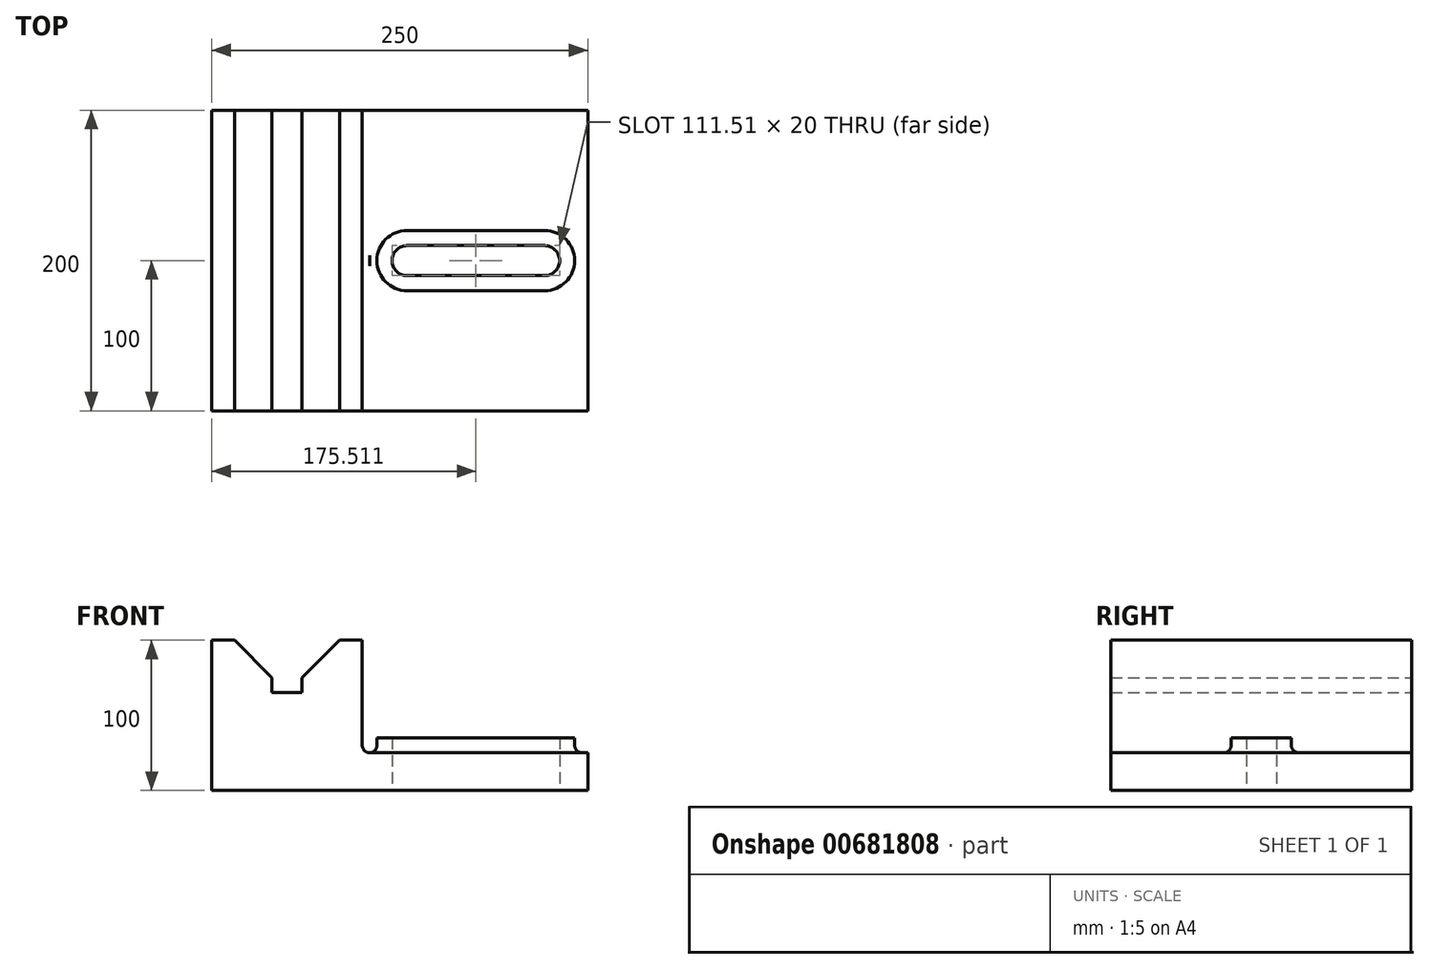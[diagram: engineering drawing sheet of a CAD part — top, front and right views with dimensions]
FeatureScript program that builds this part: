
annotation { "Feature Type Name" : "Feature", "Feature Type Description" : "" }
export const myFeature = defineFeature(function(context is Context, id is Id, definition is map)
    precondition{}
    {
        {
            var Q0;
            Q0=qCreatedBy(makeId("Front.planeOp"),FACE);
            var sketch = newSketch(context, id + "F0", { "sketchPlane" : qUnion([Q0])});
            skLineSegment(sketch, "E0", {"start": v(0, 0) * mm, "end": v(-250, 0) * mm});
            skLineSegment(sketch, "E1", {"start": v(-250, 0) * mm, "end": v(-250, 100) * mm});
            skLineSegment(sketch, "E2", {"start": v(-250, 100) * mm, "end": v(-235, 100) * mm});
            skLineSegment(sketch, "E3", {"start": v(-235, 100) * mm, "end": v(-210, 75) * mm});
            skLineSegment(sketch, "E4", {"start": v(-210, 75) * mm, "end": v(-210, 65) * mm});
            skLineSegment(sketch, "E5", {"start": v(-210, 65) * mm, "end": v(-190, 65) * mm});
            skLineSegment(sketch, "E6", {"start": v(-190, 65) * mm, "end": v(-190, 75) * mm});
            skLineSegment(sketch, "E7", {"start": v(-190, 75) * mm, "end": v(-165, 100) * mm});
            skLineSegment(sketch, "E8", {"start": v(-165, 100) * mm, "end": v(-150, 100) * mm});
            skLineSegment(sketch, "E9", {"start": v(-150, 100) * mm, "end": v(-150, 25) * mm});
            skLineSegment(sketch, "E10", {"start": v(-150, 25) * mm, "end": v(0, 25) * mm});
            skLineSegment(sketch, "E11", {"start": v(0, 25) * mm, "end": v(0, 0) * mm});
            skLineSegment(sketch, "E12", {"start": v(-210, 75) * mm, "end": v(-250, 75) * mm, "construction": true});
            skSolve(sketch);
        }
        {
            var Q0;
            Q0 = qSketchRegion(id + "F0", true);
            extrude(context, id + "F1", {"entities" : qUnion([Q0]), "depth" : 200 * mm, "offsetDistance" : 25 * mm});
        }
        {
            var Q0;
            Q0=makeQuery(id+"F1.opExtrude","SWEPT_FACE",FACE,{"disambiguationData":[OSD([sQuery(id+"F0.wireOp",EDGE,"E10")])]});
            var sketch = newSketch(context, id + "F2", { "sketchPlane" : qUnion([Q0])});
            skPoint(sketch, "E13", {"position": v(0, -100) * mm});
            skArc(sketch, "E14", {"start": v(-28.73, -110) * mm, "mid": v(-18.73, -100) * mm, "end": v(-28.73, -90) * mm});
            skArc(sketch, "E15", {"start": v(-28.73, -120) * mm, "mid": v(-8.73, -100) * mm, "end": v(-28.73, -80) * mm});
            skArc(sketch, "E16", {"start": v(-120.25, -90) * mm, "mid": v(-130.25, -100) * mm, "end": v(-120.25, -110) * mm});
            skArc(sketch, "E17", {"start": v(-120.25, -80) * mm, "mid": v(-140.25, -100) * mm, "end": v(-120.25, -120) * mm});
            skLineSegment(sketch, "E18", {"start": v(-120.25, -80) * mm, "end": v(-28.73, -80) * mm});
            skLineSegment(sketch, "E19", {"start": v(-120.25, -120) * mm, "end": v(-28.73, -120) * mm});
            skLineSegment(sketch, "E20", {"start": v(-120.25, -90) * mm, "end": v(-28.73, -90) * mm});
            skLineSegment(sketch, "E21", {"start": v(-120.25, -110) * mm, "end": v(-28.73, -110) * mm});
            skSolve(sketch);
        }
        {
            var Q0;
            Q0 = qSketchRegion(id + "F2", true);
            extrude(context, id + "F3", {"entities" : qUnion([Q0]), "operationType" : NewBodyOperationType.ADD, "depth" : 10 * mm, "offsetDistance" : 25 * mm});
        }
        {
            var Q0;
            Q0=makeQuery(id+"F3.boolean.opBoolean","SPLIT",FACE,{"disambiguationData":[TD([makeQuery(id+"F3.opExtrude","SWEPT_FACE",FACE,{"disambiguationData":[OSD([sQuery(id+"F2.wireOp",EDGE,"E14")])]})])],"derivedFrom":makeQuery(id+"F1.opExtrude","SWEPT_FACE",FACE,{"disambiguationData":[OSD([sQuery(id+"F0.wireOp",EDGE,"E10")])]})});
            extrude(context, id + "F4", {"entities" : qUnion([Q0]), "operationType" : NewBodyOperationType.REMOVE, "oppositeDirection" : true, "depth" : 25 * mm, "offsetDistance" : 25 * mm});
        }
        {
            var Q0;
            Q0=makeQuery(id+"F1.opExtrude","SWEPT_EDGE",EDGE,{"disambiguationData":[OSD([sQuery(id+"F0.wireOp",EDGE,"E9"),sQuery(id+"F0.wireOp",EDGE,"E10")])]});
            var Q1;
            Q1=makeQuery(id+"F3.opExtrude","CAP_EDGE",EDGE,{"disambiguationData":[OSD([sQuery(id+"F2.wireOp",EDGE,"E19")])],"isStart":true});
            var Q2;
            Q2=makeQuery(id+"F3.opExtrude","CAP_EDGE",EDGE,{"disambiguationData":[OSD([sQuery(id+"F2.wireOp",EDGE,"E15")])],"isStart":true});
            fillet(context, id + "F5", {"entities" : qUnion([Q0, Q1, Q2]), "radius" : 5 * mm, "tangentPropagation" : true, "allowEdgeOverflow" : false});
        }
    });
